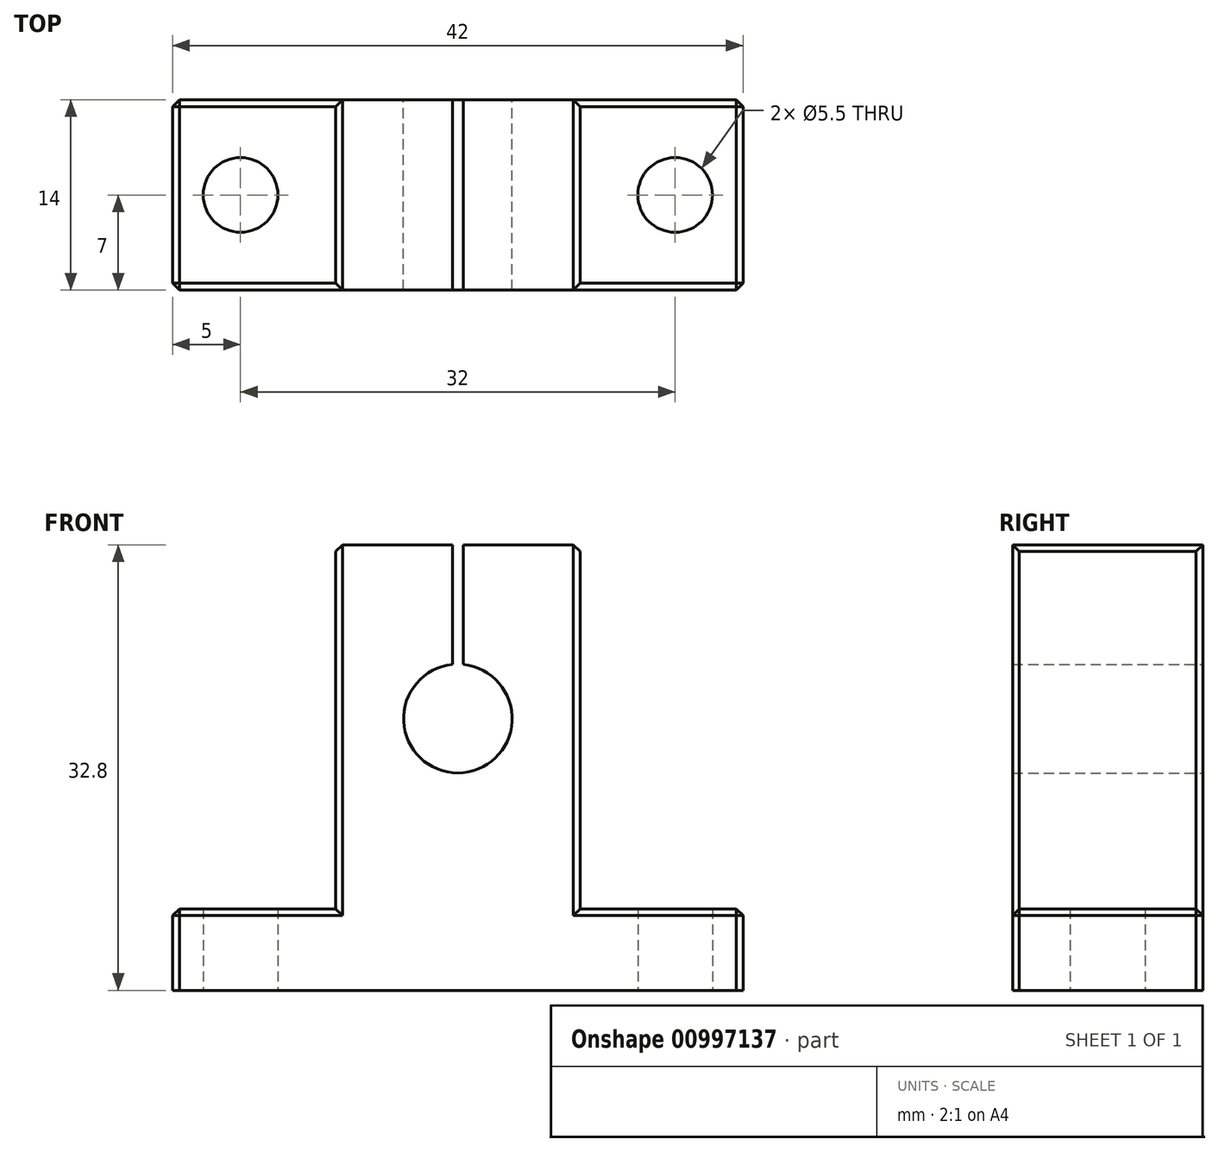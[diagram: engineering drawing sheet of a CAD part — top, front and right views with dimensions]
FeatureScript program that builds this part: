
annotation { "Feature Type Name" : "Feature", "Feature Type Description" : "" }
export const myFeature = defineFeature(function(context is Context, id is Id, definition is map)
    precondition{}
    {
        {
            var Q0;
            Q0=qCreatedBy(makeId("Front.planeOp"),FACE);
            var sketch = newSketch(context, id + "F0", { "sketchPlane" : qUnion([Q0])});
            skLineSegment(sketch, "E0.bottom", {"start": v(-21, -16.4) * mm, "end": v(21, -16.4) * mm});
            skLineSegment(sketch, "E0.top", {"start": v(-21, 16.4) * mm, "end": v(21, 16.4) * mm});
            skLineSegment(sketch, "E0.left", {"start": v(-21, -16.4) * mm, "end": v(-21, 16.4) * mm});
            skLineSegment(sketch, "E0.right", {"start": v(21, -16.4) * mm, "end": v(21, 16.4) * mm});
            skLineSegment(sketch, "E1", {"start": v(0, -16.4) * mm, "end": v(0, 16.4) * mm, "construction": true});
            skLineSegment(sketch, "E2", {"start": v(-21, -10.4) * mm, "end": v(-9, -10.4) * mm});
            skLineSegment(sketch, "E3", {"start": v(-9, -10.4) * mm, "end": v(-9, 16.4) * mm});
            skLineSegment(sketch, "E4", {"start": v(-9, 16.4) * mm, "end": v(9, 16.4) * mm});
            skLineSegment(sketch, "E5", {"start": v(9, 16.4) * mm, "end": v(9, -10.4) * mm});
            skLineSegment(sketch, "E6", {"start": v(9, -10.4) * mm, "end": v(21, -10.4) * mm});
            skLineSegment(sketch, "E7", {"start": v(-21, 0) * mm, "end": v(21, 0) * mm, "construction": true});
            skCircle(sketch, "E8", {"center": v(0, 3.6) * mm, "radius": 4 * mm});
            skLineSegment(sketch, "E9.bottom", {"start": v(-0.4, 3.6) * mm, "end": v(0.4, 3.6) * mm});
            skLineSegment(sketch, "E9.top", {"start": v(-0.4, 16.4) * mm, "end": v(0.4, 16.4) * mm});
            skLineSegment(sketch, "E9.left", {"start": v(-0.4, 3.6) * mm, "end": v(-0.4, 16.4) * mm});
            skLineSegment(sketch, "E9.right", {"start": v(0.4, 3.6) * mm, "end": v(0.4, 16.4) * mm});
            skSolve(sketch);
        }
        {
            var Q0;
            {var subQ10=sQuery(id+"F0.wireOp",EDGE,"E0.bottom");Q0=makeQuery(id+"F0.imprint","IMPRINT",FACE,{"disambiguationData":[TD([[makeQuery(id+"F0.imprint","IMPRINT",EDGE,{"derivedFrom":subQ10}),1.0]])]});}
            extrude(context, id + "F1", {"entities" : qUnion([Q0]), "depth" : 14 * mm, "offsetDistance" : 25 * mm});
        }
        {
            var Q0;
            Q0=makeQuery(id+"F1.opExtrude","SWEPT_FACE",FACE,{"disambiguationData":[OSD([sQuery(id+"F0.wireOp",EDGE,"E0.bottom")])]});
            var sketch = newSketch(context, id + "F2", { "sketchPlane" : qUnion([Q0])});
            skCircle(sketch, "E10", {"center": v(-16, 7) * mm, "radius": 2.75 * mm});
            skCircle(sketch, "E11", {"center": v(16, 7) * mm, "radius": 2.75 * mm});
            skLineSegment(sketch, "E12", {"start": v(-21, 7) * mm, "end": v(21, 7) * mm, "construction": true});
            skLineSegment(sketch, "E13", {"start": v(0, 14) * mm, "end": v(0, 0) * mm, "construction": true});
            skSolve(sketch);
        }
        {
            var Q0;
            Q0=makeQuery(id+"F2.imprint","IMPRINT",FACE,{"disambiguationData":[TD([[makeQuery(id+"F2.imprint","IMPRINT",EDGE,{"derivedFrom":sQuery(id+"F2.wireOp",EDGE,"E10")}),1.0]])]});
            var Q1;
            Q1=makeQuery(id+"F2.imprint","IMPRINT",FACE,{"disambiguationData":[TD([[makeQuery(id+"F2.imprint","IMPRINT",EDGE,{"derivedFrom":sQuery(id+"F2.wireOp",EDGE,"E11")}),1.0]])]});
            extrude(context, id + "F3", {"entities" : qUnion([Q0, Q1]), "operationType" : NewBodyOperationType.REMOVE, "oppositeDirection" : true, "depth" : 6 * mm, "offsetDistance" : 25 * mm});
        }
        {
            var Q0;
            Q0=makeQuery(id+"F1.opExtrude","SWEPT_EDGE",EDGE,{"disambiguationData":[OSD([sQuery(id+"F0.wireOp",EDGE,"E0.top"),sQuery(id+"F0.wireOp",EDGE,"E4"),sQuery(id+"F0.wireOp",EDGE,"E5")])]});
            var Q1;
            {var subQ0=sQuery(id+"F0.wireOp",EDGE,"E4");Q1=makeQuery(id+"F1.opExtrude","CAP_EDGE",EDGE,{"disambiguationData":[OSD([subQ0]),TDD([makeQuery(id+"F0.imprint","IMPRINT",EDGE,{"disambiguationData":[TD([[makeQuery(id+"F0.imprint","INTERSECT",VERTEX,{"derivedFrom":[sQuery(id+"F0.wireOp",EDGE,"E0.top"),subQ0,sQuery(id+"F0.wireOp",EDGE,"E5")]}),1.0]])],"derivedFrom":subQ0})])],"isStart":false});}
            var Q2;
            {var subQ0=sQuery(id+"F0.wireOp",EDGE,"E4");Q2=makeQuery(id+"F1.opExtrude","CAP_EDGE",EDGE,{"disambiguationData":[OSD([subQ0]),TDD([makeQuery(id+"F0.imprint","IMPRINT",EDGE,{"disambiguationData":[TD([[makeQuery(id+"F0.imprint","INTERSECT",VERTEX,{"derivedFrom":[sQuery(id+"F0.wireOp",EDGE,"E0.top"),subQ0,sQuery(id+"F0.wireOp",EDGE,"E5")]}),1.0]])],"derivedFrom":subQ0})])],"isStart":true});}
            var Q3;
            {var subQ0=sQuery(id+"F0.wireOp",EDGE,"E4");Q3=makeQuery(id+"F1.opExtrude","CAP_EDGE",EDGE,{"disambiguationData":[OSD([subQ0]),TDD([makeQuery(id+"F0.imprint","IMPRINT",EDGE,{"disambiguationData":[TD([[makeQuery(id+"F0.imprint","INTERSECT",VERTEX,{"derivedFrom":[sQuery(id+"F0.wireOp",EDGE,"E0.top"),sQuery(id+"F0.wireOp",EDGE,"E3"),subQ0]}),-1.0]])],"derivedFrom":subQ0})])],"isStart":false});}
            var Q4;
            Q4=makeQuery(id+"F1.opExtrude","SWEPT_EDGE",EDGE,{"disambiguationData":[OSD([sQuery(id+"F0.wireOp",EDGE,"E0.top"),sQuery(id+"F0.wireOp",EDGE,"E3"),sQuery(id+"F0.wireOp",EDGE,"E4")])]});
            var Q5;
            {var subQ0=sQuery(id+"F0.wireOp",EDGE,"E4");Q5=makeQuery(id+"F1.opExtrude","CAP_EDGE",EDGE,{"disambiguationData":[OSD([subQ0]),TDD([makeQuery(id+"F0.imprint","IMPRINT",EDGE,{"disambiguationData":[TD([[makeQuery(id+"F0.imprint","INTERSECT",VERTEX,{"derivedFrom":[sQuery(id+"F0.wireOp",EDGE,"E0.top"),sQuery(id+"F0.wireOp",EDGE,"E3"),subQ0]}),-1.0]])],"derivedFrom":subQ0})])],"isStart":true});}
            var Q6;
            Q6=makeQuery(id+"F1.opExtrude","CAP_EDGE",EDGE,{"disambiguationData":[OSD([sQuery(id+"F0.wireOp",EDGE,"E5")])],"isStart":false});
            var Q7;
            Q7=makeQuery(id+"F1.opExtrude","CAP_EDGE",EDGE,{"disambiguationData":[OSD([sQuery(id+"F0.wireOp",EDGE,"E5")])],"isStart":true});
            var Q8;
            Q8=makeQuery(id+"F1.opExtrude","CAP_EDGE",EDGE,{"disambiguationData":[OSD([sQuery(id+"F0.wireOp",EDGE,"E6")])],"isStart":true});
            var Q9;
            Q9=makeQuery(id+"F1.opExtrude","CAP_EDGE",EDGE,{"disambiguationData":[OSD([sQuery(id+"F0.wireOp",EDGE,"E6")])],"isStart":false});
            var Q10;
            Q10=makeQuery(id+"F1.opExtrude","SWEPT_EDGE",EDGE,{"disambiguationData":[OSD([sQuery(id+"F0.wireOp",EDGE,"E0.right"),sQuery(id+"F0.wireOp",EDGE,"E6")])]});
            var Q11;
            Q11=makeQuery(id+"F1.opExtrude","CAP_EDGE",EDGE,{"disambiguationData":[OSD([sQuery(id+"F0.wireOp",EDGE,"E0.right")])],"isStart":false});
            var Q12;
            Q12=makeQuery(id+"F1.opExtrude","CAP_EDGE",EDGE,{"disambiguationData":[OSD([sQuery(id+"F0.wireOp",EDGE,"E0.right")])],"isStart":true});
            var Q13;
            Q13=makeQuery(id+"F1.opExtrude","CAP_EDGE",EDGE,{"disambiguationData":[OSD([sQuery(id+"F0.wireOp",EDGE,"E3")])],"isStart":false});
            var Q14;
            Q14=makeQuery(id+"F1.opExtrude","CAP_EDGE",EDGE,{"disambiguationData":[OSD([sQuery(id+"F0.wireOp",EDGE,"E2")])],"isStart":false});
            var Q15;
            Q15=makeQuery(id+"F1.opExtrude","CAP_EDGE",EDGE,{"disambiguationData":[OSD([sQuery(id+"F0.wireOp",EDGE,"E0.left")])],"isStart":false});
            var Q16;
            Q16=makeQuery(id+"F1.opExtrude","SWEPT_EDGE",EDGE,{"disambiguationData":[OSD([sQuery(id+"F0.wireOp",EDGE,"E0.left"),sQuery(id+"F0.wireOp",EDGE,"E2")])]});
            var Q17;
            Q17=makeQuery(id+"F1.opExtrude","CAP_EDGE",EDGE,{"disambiguationData":[OSD([sQuery(id+"F0.wireOp",EDGE,"E3")])],"isStart":true});
            var Q18;
            Q18=makeQuery(id+"F1.opExtrude","CAP_EDGE",EDGE,{"disambiguationData":[OSD([sQuery(id+"F0.wireOp",EDGE,"E2")])],"isStart":true});
            var Q19;
            Q19=makeQuery(id+"F1.opExtrude","CAP_EDGE",EDGE,{"disambiguationData":[OSD([sQuery(id+"F0.wireOp",EDGE,"E0.left")])],"isStart":true});
            chamfer(context, id + "F4", {"entities" : qUnion([Q0, Q1, Q2, Q3, Q4, Q5, Q6, Q7, Q8, Q9, Q10, Q11, Q12, Q13, Q14, Q15, Q16, Q17, Q18, Q19]), "width" : 0.5 * mm, "tangentPropagation" : true});
        }
    });
